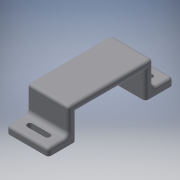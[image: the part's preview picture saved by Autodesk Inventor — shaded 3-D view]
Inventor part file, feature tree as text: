
AUTODESK INVENTOR PART (.ipt)
format: ipt  version: 2016 (Build 200138000, 138)  size: 183,296 bytes
history: native  units: mm
features: extrude x2, fillet x2, sketch x2, projected_geometry x1
ambient origin geometry x8: Origin, YZ Plane, XZ Plane, XY Plane, X Axis, Y Axis, Z Axis, Center Point
bodies: Solid1 (feature_tree)
feature tree (7):
  extrude  "Extrusion1"  Depth=30.0mm
  extrude  "Extrusion2"  Depth=8.0mm
  fillet  "Fillet1"  Radius=8.0mm
  fillet  "Fillet2"  Radius=8.0mm
  sketch  "Sketch1"  dims[d0=75.0mm d1=30.0mm]
  sketch  "Sketch2"  dims[d2=8.0mm d3=8.0mm d4=8.0mm d5=8.0mm d6=28.0mm d7=45.0mm d8=0.0mm d9=45.0mm d10=0.0mm d11=5.0mm d12=3.0mm]
  projected_geometry  "Projected Loop1"
